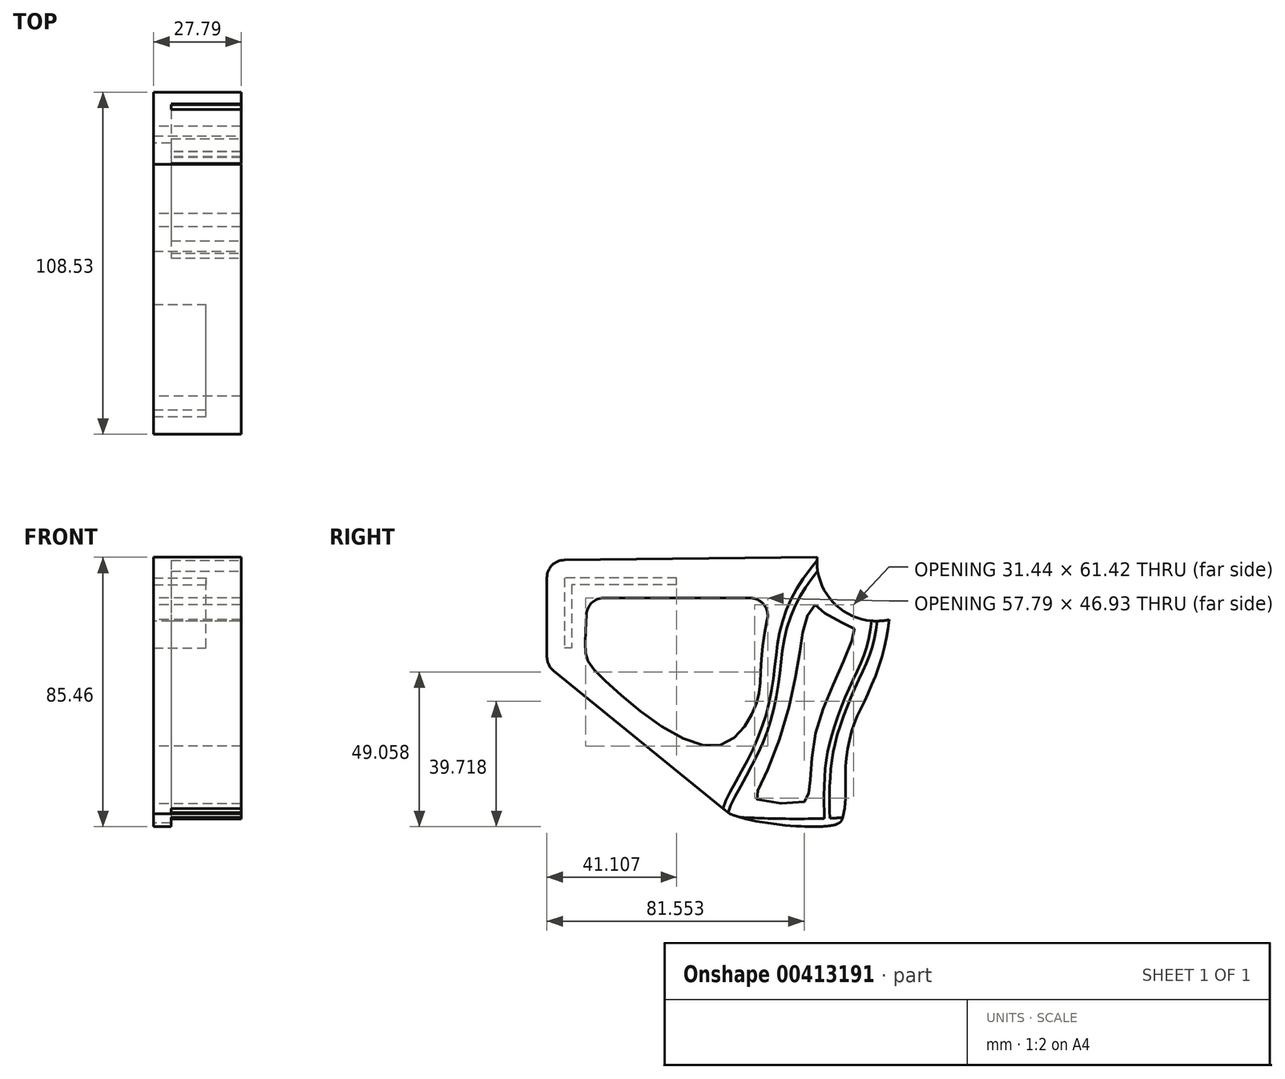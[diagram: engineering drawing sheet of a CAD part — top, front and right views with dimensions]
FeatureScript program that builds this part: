
annotation { "Feature Type Name" : "Feature", "Feature Type Description" : "" }
export const myFeature = defineFeature(function(context is Context, id is Id, definition is map)
    precondition{}
    {
        {
            var Q0;
            Q0=qCreatedBy(makeId("Right.planeOp"),FACE);
            var sketch = newSketch(context, id + "F0", { "sketchPlane" : qUnion([Q0])});
            skCircle(sketch, "E0", {"center": v(-31.04, 31) * mm, "radius": 17 * mm});
            skSolve(sketch);
        }
        {
            var Q0;
            Q0 = qSketchRegion(id + "F0", true);
            extrude(context, id + "F1", {"entities" : qUnion([Q0]), "depth" : 50 * mm});
        }
        {
            var Q0;
            Q0=makeQuery(id+"F1.opExtrude","CAP_FACE",FACE,{"disambiguationData":[OSD([sQuery(id+"F0.wireOp",EDGE,"E0")])],"isStart":false});
            var sketch = newSketch(context, id + "F2", { "sketchPlane" : qUnion([Q0])});
            skFitSpline(sketch, "E1", {"points": [v(-14.08, 32.2) * mm, v(-3.53, 18.57) * mm, v(6.67, -3.26) * mm, v(13.85, -14.17) * mm, v(18.44, -18.92) * mm], "startDerivative": vector(40.33, -44.23) * mm, "endDerivative": vector(27.26, -23.06) * mm});
            skFitSpline(sketch, "E2", {"points": [v(-23.58, 15.73) * mm, v(-20.2, 7.66) * mm, v(-14.6, 0) * mm, v(-10.28, -5.13) * mm, v(-5.4, -12.74) * mm, v(-2.38, -19.78) * mm, v(0, -26.81) * mm, v(0, -34.57) * mm], "startDerivative": vector(18.93, -54.47) * mm, "endDerivative": vector(-4.52, -54.23) * mm});
            skFitSpline(sketch, "E3", {"points": [v(-32.4, 14.06) * mm, v(-33.98, 6.08) * mm, v(-37.14, -1.54) * mm, v(-41.16, -10.73) * mm, v(-44.32, -20.35) * mm, v(-45.62, -27.82) * mm, v(-46.05, -36) * mm, v(-45.89, -42.3) * mm], "startDerivative": vector(-8.4, -57.3) * mm, "endDerivative": vector(1.97, -45.55) * mm});
            skFitSpline(sketch, "E4", {"points": [v(-15.37, 31.23) * mm, v(-4.82, 17.6) * mm, v(5.37, -4.23) * mm, v(12.56, -15.15) * mm, v(17.37, -20.19) * mm], "startDerivative": vector(40.33, -44.23) * mm, "endDerivative": vector(27.26, -23.06) * mm});
            skFitSpline(sketch, "E5", {"points": [v(-25.27, 15.4) * mm, v(-21.88, 7.33) * mm, v(-16.28, -0.33) * mm, v(-11.97, -5.46) * mm, v(-7.09, -13.07) * mm, v(-4.07, -20.1) * mm, v(-1.69, -27.14) * mm, v(-1.39, -35.19) * mm], "startDerivative": vector(18.93, -54.47) * mm, "endDerivative": vector(-4.52, -54.23) * mm});
            skFitSpline(sketch, "E6", {"points": [v(-30.83, 14) * mm, v(-32.4, 6.02) * mm, v(-35.56, -1.6) * mm, v(-39.58, -10.79) * mm, v(-42.74, -20.41) * mm, v(-44.03, -27.88) * mm, v(-44.47, -36.07) * mm, v(-44.32, -42.25) * mm], "startDerivative": vector(-8.4, -57.3) * mm, "endDerivative": vector(1.97, -45.55) * mm});
            skFitSpline(sketch, "E7", {"points": [v(-48.04, 31.37) * mm, v(-54.23, 22.45) * mm, v(-58.4, 11.97) * mm, v(-59.98, 1.48) * mm, v(-61.85, -10) * mm, v(-65.87, -21.64) * mm, v(-71.47, -32.27) * mm, v(-74.77, -39.31) * mm, v(-74.9, -41.76) * mm], "startDerivative": vector(-49.06, -63.68) * mm, "endDerivative": vector(1.83, -30.25) * mm});
            skFitSpline(sketch, "E8", {"points": [v(-47.82, 28.3) * mm, v(-52.73, 21.35) * mm, v(-56.9, 10.87) * mm, v(-58.48, 0.38) * mm, v(-60.35, -11.1) * mm, v(-64.37, -22.74) * mm, v(-69.97, -33.37) * mm, v(-73.3, -40.4) * mm, v(-73.4, -42.42) * mm], "startDerivative": vector(-49.06, -63.68) * mm, "endDerivative": vector(1.83, -30.25) * mm});
            skLineSegment(sketch, "E9", {"start": v(-32.4, 14.06) * mm, "end": v(-30.83, 14) * mm});
            skLineSegment(sketch, "E10", {"start": v(-23.58, 15.73) * mm, "end": v(-25.12, 14.98) * mm});
            skLineSegment(sketch, "E11", {"start": v(-14.08, 32.2) * mm, "end": v(-13.9, 29.61) * mm});
            skLineSegment(sketch, "E12", {"start": v(18.44, -18.92) * mm, "end": v(17.37, -20.19) * mm});
            skLineSegment(sketch, "E13", {"start": v(0, -34.57) * mm, "end": v(-1.39, -35.19) * mm});
            skLineSegment(sketch, "E14", {"start": v(-44.32, -42.25) * mm, "end": v(-45.89, -42.3) * mm});
            skLineSegment(sketch, "E15", {"start": v(-73.44, -41.83) * mm, "end": v(-74.9, -41.76) * mm});
            skLineSegment(sketch, "E16", {"start": v(-48.04, 31.37) * mm, "end": v(-47.82, 28.3) * mm});
            skFitSpline(sketch, "E17", {"points": [v(18.44, -18.92) * mm, v(0, -34.57) * mm, v(-44.32, -42.25) * mm, v(-74.9, -41.76) * mm], "startDerivative": vector(-51.9, -61.3) * mm, "endDerivative": vector(-86.85, 4.24) * mm});
            skFitSpline(sketch, "E18", {"points": [v(18.63, -22.36) * mm, v(0.18, -37.58) * mm, v(-44.14, -45.26) * mm, v(-74.72, -45.2) * mm], "startDerivative": vector(-51.9, -61.3) * mm, "endDerivative": vector(-86.85, 4.24) * mm});
            skLineSegment(sketch, "E19", {"start": v(18.63, -22.36) * mm, "end": v(18.44, -18.92) * mm});
            skLineSegment(sketch, "E20", {"start": v(-74.72, -45.2) * mm, "end": v(-74.9, -41.76) * mm});
            skSolve(sketch);
        }
        {
            var Q0;
            Q0 = qSketchRegion(id + "F2", true);
            extrude(context, id + "F3", {"entities" : qUnion([Q0]), "oppositeDirection" : true, "depth" : 25 * mm});
        }
        {
            var Q0;
            Q0=makeQuery(id+"F3.opExtrude","CAP_FACE",FACE,{"disambiguationData":[OSD([sQuery(id+"F2.wireOp",EDGE,"E1"),sQuery(id+"F2.wireOp",EDGE,"E2"),sQuery(id+"F2.wireOp",EDGE,"E3"),sQuery(id+"F2.wireOp",EDGE,"E4"),sQuery(id+"F2.wireOp",EDGE,"E5"),sQuery(id+"F2.wireOp",EDGE,"E6"),sQuery(id+"F2.wireOp",EDGE,"E7"),sQuery(id+"F2.wireOp",EDGE,"E8"),sQuery(id+"F2.wireOp",EDGE,"E9"),sQuery(id+"F2.wireOp",EDGE,"E10"),sQuery(id+"F2.wireOp",EDGE,"E11"),sQuery(id+"F2.wireOp",EDGE,"E16"),sQuery(id+"F2.wireOp",EDGE,"E17"),sQuery(id+"F2.wireOp",EDGE,"E18"),sQuery(id+"F2.wireOp",EDGE,"E19"),sQuery(id+"F2.wireOp",EDGE,"E20")])],"isStart":false});
            cPlane(context, id + "F4", {"entities" : qUnion([Q0]), "cplaneType" : CPlaneType.OFFSET, "offset" : 10 * mm, "oppositeDirection" : true, "width" : 150 * mm, "height" : 150 * mm});
        }
        {
            var Q0;
            Q0=qCreatedBy(id+"F4.planeOp",FACE);
            var sketch = newSketch(context, id + "F5", { "sketchPlane" : qUnion([Q0])});
            skPoint(sketch, "E21", {"position": v(48.04, 31.37) * mm});
            skLineSegment(sketch, "E22", {"start": v(31.15, 97.47) * mm, "end": v(31.15, -54.75) * mm, "construction": true});
            skLineSegment(sketch, "E23.MirrorCS", {"start": v(120.04, 26.37) * mm, "end": v(88.04, 26.37) * mm});
            skLineSegment(sketch, "E24.MirrorCS", {"start": v(118.04, 24.37) * mm, "end": v(88.04, 24.37) * mm});
            skLineSegment(sketch, "E25.MirrorCS", {"start": v(88.04, 26.37) * mm, "end": v(88.04, 24.37) * mm});
            skLineSegment(sketch, "E26.MirrorCS", {"start": v(120.04, 6.37) * mm, "end": v(120.04, 26.37) * mm});
            skLineSegment(sketch, "E27.MirrorCS", {"start": v(118.04, 6.37) * mm, "end": v(118.04, 24.37) * mm});
            skLineSegment(sketch, "E28.MirrorCS", {"start": v(120.04, 6.37) * mm, "end": v(118.04, 6.37) * mm});
            skSolve(sketch);
        }
        {
            var Q0;
            Q0 = qSketchRegion(id + "F5", true);
            extrude(context, id + "F6", {"entities" : qUnion([Q0]), "depth" : 50 * mm});
        }
        {
            var Q0;
            Q0=makeQuery(id+"F3.opExtrude","CAP_FACE",FACE,{"disambiguationData":[OSD([sQuery(id+"F2.wireOp",EDGE,"E1"),sQuery(id+"F2.wireOp",EDGE,"E2"),sQuery(id+"F2.wireOp",EDGE,"E3"),sQuery(id+"F2.wireOp",EDGE,"E4"),sQuery(id+"F2.wireOp",EDGE,"E5"),sQuery(id+"F2.wireOp",EDGE,"E6"),sQuery(id+"F2.wireOp",EDGE,"E7"),sQuery(id+"F2.wireOp",EDGE,"E8"),sQuery(id+"F2.wireOp",EDGE,"E9"),sQuery(id+"F2.wireOp",EDGE,"E10"),sQuery(id+"F2.wireOp",EDGE,"E11"),sQuery(id+"F2.wireOp",EDGE,"E16"),sQuery(id+"F2.wireOp",EDGE,"E17"),sQuery(id+"F2.wireOp",EDGE,"E18"),sQuery(id+"F2.wireOp",EDGE,"E19"),sQuery(id+"F2.wireOp",EDGE,"E20")])],"isStart":false});
            cPlane(context, id + "F7", {"entities" : qUnion([Q0]), "cplaneType" : CPlaneType.OFFSET, "offset" : 5 * mm, "width" : 150 * mm, "height" : 150 * mm});
        }
        {
            var Q0;
            Q0=qCreatedBy(id+"F7.planeOp",FACE);
            var sketch = newSketch(context, id + "F8", { "sketchPlane" : qUnion([Q0])});
            skFitSpline(sketch, "E29", {"points": [v(27.28, 15.63) * mm, v(37.87, 18.6) * mm, v(44.65, 32.27) * mm], "startDerivative": vector(46.52, 0.04) * mm, "endDerivative": vector(8.6, 49.94) * mm});
            skFitSpline(sketch, "E30", {"points": [v(27.28, 15.63) * mm, v(29.56, 3.66) * mm, v(34.24, -8.3) * mm, v(37.88, -16.63) * mm, v(39.83, -27.33) * mm, v(39.9, -35.78) * mm, v(41.96, -43.62) * mm], "startDerivative": vector(5.92, -60.27) * mm, "endDerivative": vector(30.93, 0) * mm});
            skFitSpline(sketch, "E31", {"points": [v(41.96, -43.62) * mm, v(72.85, -41.02) * mm], "startDerivative": vector(2.26, -5.16) * mm, "endDerivative": vector(33.87, 12.42) * mm});
            skLineSegment(sketch, "E32", {"start": v(72.85, -41.02) * mm, "end": v(125.04, 1.37) * mm});
            skLineSegment(sketch, "E33", {"start": v(125.04, 1.37) * mm, "end": v(125.04, 31.37) * mm});
            skLineSegment(sketch, "E34", {"start": v(125.04, 31.37) * mm, "end": v(44.65, 32.27) * mm});
            skFitSpline(sketch, "E35", {"points": [v(60.36, 20.6) * mm, v(63.37, 8.38) * mm, v(64.23, -3.35) * mm, v(66.17, -11.64) * mm, v(78.14, -21.62) * mm, v(110.22, -1.24) * mm, v(114.06, 5.2) * mm, v(113.73, 20.6) * mm], "startDerivative": vector(28.36, -78.83) * mm, "endDerivative": vector(1.04, 137.92) * mm});
            skLineSegment(sketch, "E36", {"start": v(60.36, 20.6) * mm, "end": v(113.73, 20.6) * mm});
            skFitSpline(sketch, "E37", {"points": [v(48.6, 18.7) * mm, v(44.72, 15.29) * mm, v(37.65, 12.21) * mm, v(37.54, 9.82) * mm, v(42.44, -2.04) * mm, v(48.37, -17.77) * mm, v(49.97, -31.45) * mm, v(50.42, -35.78) * mm, v(51.79, -37.6) * mm, v(65.47, -36.7) * mm, v(65.01, -34.42) * mm, v(57.15, -14.7) * mm, v(52.82, 5.94) * mm, v(51.22, 14.26) * mm, v(48.6, 18.7) * mm]});
            skFitSpline(sketch, "E38", {"points": [v(39.49, -41.88) * mm, v(51.36, -42.33) * mm, v(64.2, -42.23) * mm, v(73.23, -41.78) * mm], "startDerivative": vector(32.78, -1.67) * mm, "endDerivative": vector(27.92, 0.5) * mm});
            skSolve(sketch);
        }
        {
            var Q0;
            Q0 = qSketchRegion(id + "F8", true);
            extrude(context, id + "F9", {"entities" : qUnion([Q0]), "oppositeDirection" : true, "depth" : 25 * mm});
        }
        {
            var Q0;
            Q0=makeQuery(id+"F9.opExtrude","SWEPT_EDGE",EDGE,{"disambiguationData":[OSD([sQuery(id+"F8.wireOp",EDGE,"E33"),sQuery(id+"F8.wireOp",EDGE,"E34")])]});
            var Q1;
            Q1=makeQuery(id+"F9.opExtrude","SWEPT_EDGE",EDGE,{"disambiguationData":[OSD([sQuery(id+"F8.wireOp",EDGE,"E32"),sQuery(id+"F8.wireOp",EDGE,"E33")])]});
            var Q2;
            {var subQ0=sQuery(id+"F8.wireOp",EDGE,"E36");var subQ1=sQuery(id+"F8.wireOp",EDGE,"E35");Q2=makeQuery(id+"F9.opExtrude","SWEPT_EDGE",EDGE,{"disambiguationData":[OSD([subQ1,subQ0]),TDD([makeQuery(id+"F8.imprint","INTERSECT",VERTEX,{"disambiguationData":[OD(0.0)],"derivedFrom":[subQ1,subQ0]})])]});}
            var Q3;
            {var subQ0=sQuery(id+"F8.wireOp",EDGE,"E36");var subQ1=sQuery(id+"F8.wireOp",EDGE,"E35");Q3=makeQuery(id+"F9.opExtrude","SWEPT_EDGE",EDGE,{"disambiguationData":[OSD([subQ1,subQ0]),TDD([makeQuery(id+"F8.imprint","INTERSECT",VERTEX,{"disambiguationData":[OD(1.0)],"derivedFrom":[subQ1,subQ0]})])]});}
            fillet(context, id + "F10", {"entities" : qUnion([Q0, Q1, Q2, Q3]), "radius" : 5 * mm, "tangentPropagation" : true, "allowEdgeOverflow" : false});
        }
        {
            var Q0;
            Q0=makeQuery(id+"F6.opExtrude","SWEPT_BODY",BODY,{"disambiguationData":[OSD([sQuery(id+"F5.wireOp",EDGE,"E23.MirrorCS"),sQuery(id+"F5.wireOp",EDGE,"E24.MirrorCS"),sQuery(id+"F5.wireOp",EDGE,"E25.MirrorCS"),sQuery(id+"F5.wireOp",EDGE,"E26.MirrorCS"),sQuery(id+"F5.wireOp",EDGE,"E27.MirrorCS"),sQuery(id+"F5.wireOp",EDGE,"E28.MirrorCS")])]});
            var Q1;
            Q1=makeQuery(id+"F3.opExtrude","SWEPT_BODY",BODY,{"disambiguationData":[OSD([sQuery(id+"F2.wireOp",EDGE,"E1"),sQuery(id+"F2.wireOp",EDGE,"E2"),sQuery(id+"F2.wireOp",EDGE,"E3"),sQuery(id+"F2.wireOp",EDGE,"E4"),sQuery(id+"F2.wireOp",EDGE,"E5"),sQuery(id+"F2.wireOp",EDGE,"E6"),sQuery(id+"F2.wireOp",EDGE,"E7"),sQuery(id+"F2.wireOp",EDGE,"E8"),sQuery(id+"F2.wireOp",EDGE,"E9"),sQuery(id+"F2.wireOp",EDGE,"E10"),sQuery(id+"F2.wireOp",EDGE,"E11"),sQuery(id+"F2.wireOp",EDGE,"E16"),sQuery(id+"F2.wireOp",EDGE,"E17"),sQuery(id+"F2.wireOp",EDGE,"E18"),sQuery(id+"F2.wireOp",EDGE,"E19"),sQuery(id+"F2.wireOp",EDGE,"E20")])]});
            var Q2;
            Q2=makeQuery(id+"F1.opExtrude","SWEPT_BODY",BODY,{"disambiguationData":[OSD([sQuery(id+"F0.wireOp",EDGE,"E0")])]});
            var Q3;
            Q3=makeQuery(id+"F9.opExtrude","SWEPT_BODY",BODY,{"disambiguationData":[OSD([sQuery(id+"F8.wireOp",EDGE,"E29"),sQuery(id+"F8.wireOp",EDGE,"E30"),sQuery(id+"F8.wireOp",EDGE,"E31"),sQuery(id+"F8.wireOp",EDGE,"E32"),sQuery(id+"F8.wireOp",EDGE,"E33"),sQuery(id+"F8.wireOp",EDGE,"E34"),sQuery(id+"F8.wireOp",EDGE,"E35"),sQuery(id+"F8.wireOp",EDGE,"E36"),sQuery(id+"F8.wireOp",EDGE,"E37"),sQuery(id+"F8.wireOp",EDGE,"E38")])]});
            booleanBodies(context, id + "F11", {"operationType" : BooleanOperationType.SUBTRACTION, "tools" : qUnion([Q0, Q1, Q2]), "targets" : qUnion([Q3])});
        }
        {
            var Q0;
            Q0=makeQuery(id+"F11.opBoolean","SPLIT",BODY,{"disambiguationData":[OD(1.0)],"derivedFrom":makeQuery(id+"F9.opExtrude","SWEPT_BODY",BODY,{"disambiguationData":[OSD([sQuery(id+"F8.wireOp",EDGE,"E29"),sQuery(id+"F8.wireOp",EDGE,"E30"),sQuery(id+"F8.wireOp",EDGE,"E31"),sQuery(id+"F8.wireOp",EDGE,"E32"),sQuery(id+"F8.wireOp",EDGE,"E33"),sQuery(id+"F8.wireOp",EDGE,"E34"),sQuery(id+"F8.wireOp",EDGE,"E35"),sQuery(id+"F8.wireOp",EDGE,"E36"),sQuery(id+"F8.wireOp",EDGE,"E37"),sQuery(id+"F8.wireOp",EDGE,"E38")])]})});
            var Q1;
            Q1=qCreatedBy(makeId("Origin.pointOp"),VERTEX);
            transform(context, id + "F12", {"entities" : qUnion([Q0]), "transformType" : TransformType.SCALE_UNIFORMLY, "scale" : (34 + 3.8) / 34, "scalePoint" : qUnion([Q1]), "makeCopy" : false});
        }
    });
